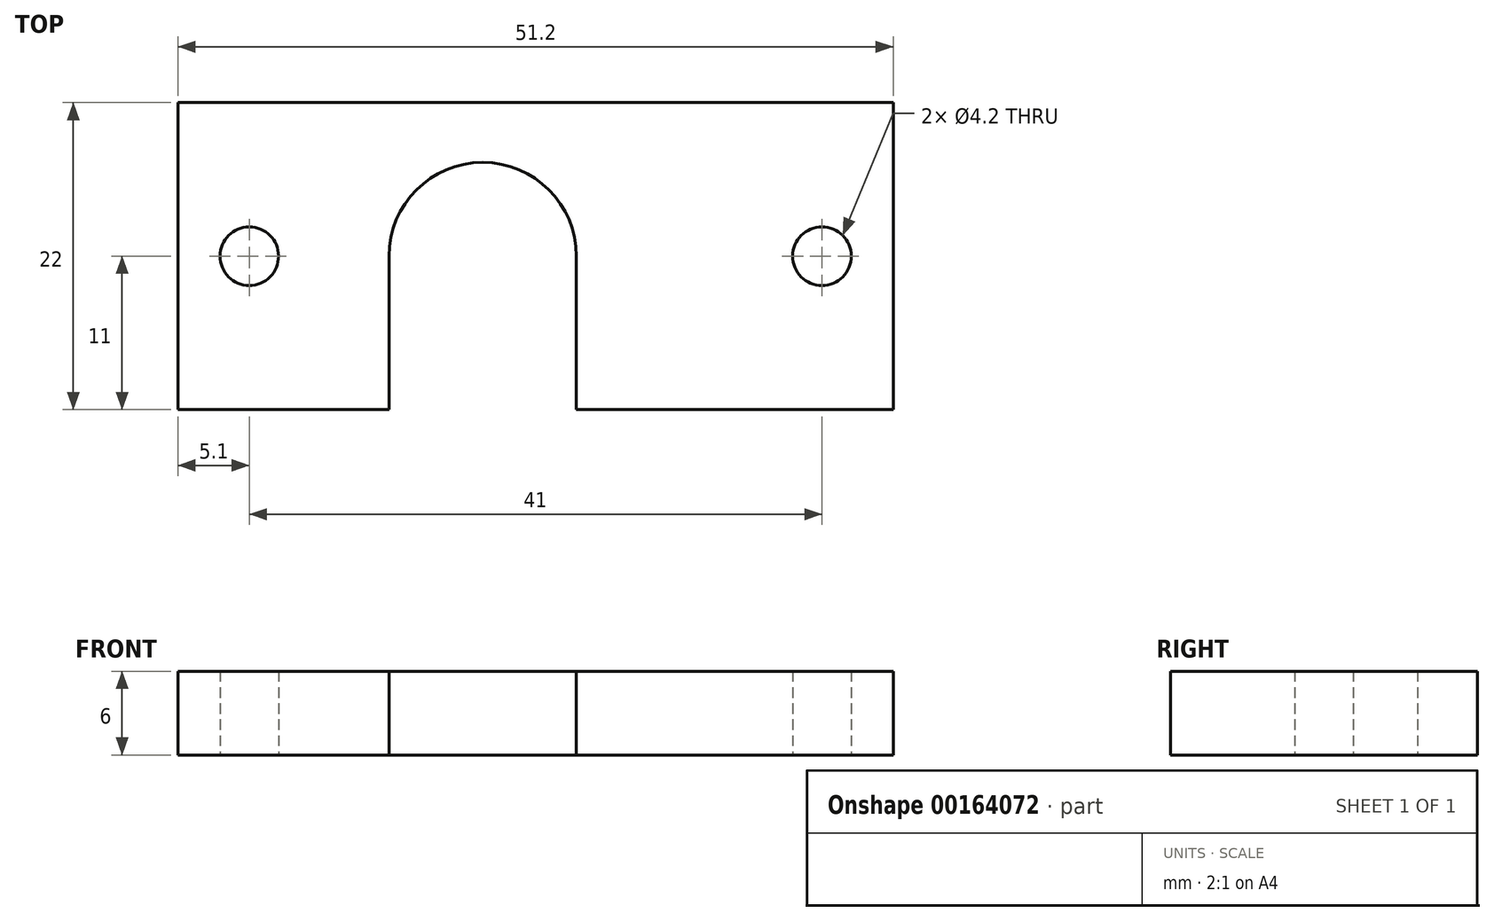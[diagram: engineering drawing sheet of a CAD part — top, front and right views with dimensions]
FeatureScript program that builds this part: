
annotation { "Feature Type Name" : "Feature", "Feature Type Description" : "" }
export const myFeature = defineFeature(function(context is Context, id is Id, definition is map)
    precondition{}
    {
        {
            var Q0;
            Q0=qCreatedBy(makeId("Top.planeOp"),FACE);
            var sketch = newSketch(context, id + "F0", { "sketchPlane" : qUnion([Q0])});
            skLineSegment(sketch, "E0.bottom", {"start": v(25.6, 11) * mm, "end": v(-25.6, 11) * mm});
            skLineSegment(sketch, "E0.top", {"start": v(25.6, -11) * mm, "end": v(-25.6, -11) * mm});
            skLineSegment(sketch, "E0.left", {"start": v(25.6, 11) * mm, "end": v(25.6, -11) * mm});
            skLineSegment(sketch, "E0.right", {"start": v(-25.6, 11) * mm, "end": v(-25.6, -11) * mm});
            skPoint(sketch, "E0.middle", {"position": v(0, 0) * mm});
            skPoint(sketch, "E1", {"position": v(-10.5, -11) * mm});
            skPoint(sketch, "E2", {"position": v(2.92, -11) * mm});
            skLineSegment(sketch, "E3", {"start": v(20.5, 11) * mm, "end": v(20.5, -11) * mm, "construction": true});
            skCircle(sketch, "E4", {"center": v(20.5, 0) * mm, "radius": 2.1 * mm});
            skLineSegment(sketch, "E5", {"start": v(-20.5, 11) * mm, "end": v(-20.5, -11) * mm, "construction": true});
            skCircle(sketch, "E6", {"center": v(-20.5, 0) * mm, "radius": 2.1 * mm});
            skPoint(sketch, "E7", {"position": v(-3.8, -11) * mm});
            skLineSegment(sketch, "E8", {"start": v(-3.8, -11) * mm, "end": v(-3.8, 0) * mm, "construction": true});
            skLineSegment(sketch, "E9", {"start": v(2.92, -11) * mm, "end": v(2.92, 0) * mm, "construction": true});
            skLineSegment(sketch, "E10.bottom", {"start": v(-10.5, -11) * mm, "end": v(2.92, -11) * mm});
            skLineSegment(sketch, "E10.top", {"start": v(-10.5, 0) * mm, "end": v(2.92, 0) * mm});
            skLineSegment(sketch, "E10.left", {"start": v(-10.5, -11) * mm, "end": v(-10.5, 0) * mm});
            skLineSegment(sketch, "E10.right", {"start": v(2.92, -11) * mm, "end": v(2.92, 0) * mm});
            skCircle(sketch, "E11", {"center": v(-3.8, 0) * mm, "radius": 6.71 * mm});
            skSolve(sketch);
        }
        {
            var Q0;
            Q0=makeQuery(id+"F0.imprint","IMPRINT",FACE,{"disambiguationData":[TD([[makeQuery(id+"F0.imprint","IMPRINT",EDGE,{"derivedFrom":sQuery(id+"F0.wireOp",EDGE,"E0.bottom")}),1.0]])]});
            extrude(context, id + "F1", {"entities" : qUnion([Q0]), "endBound" : BoundingType.SYMMETRIC, "depth" : 6 * mm, "hasSecondDirection" : true, "secondDirectionOppositeDirection" : true, "secondDirectionDepth" : 3 * mm});
        }
    });
